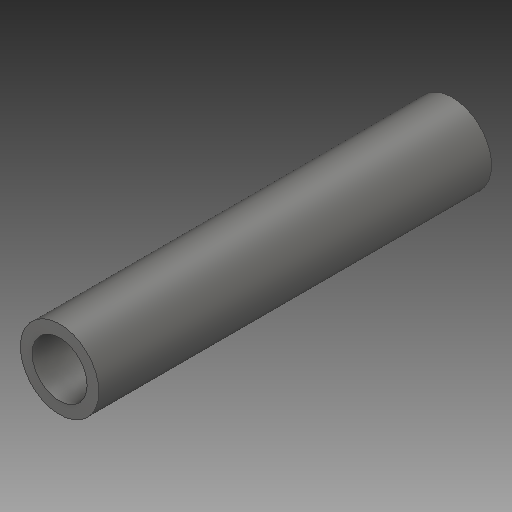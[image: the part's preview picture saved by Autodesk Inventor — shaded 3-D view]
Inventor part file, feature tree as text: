
AUTODESK INVENTOR PART (.ipt)
format: ipt  version: 2019 (Build 230136000, 136)  size: 100,864 bytes
history: native  units: in
note: dims shown in document units (in); Inventor stores cm internally (conversion verified against a paired STEP export)
features: other x3, sketch x3
ambient origin geometry x8: Origin, YZ Plane, XZ Plane, XY Plane, X Axis, Y Axis, Z Axis, Center Point
bodies: Solid1 (feature_tree)
feature tree (6):
  other  "project rolller 1 part.ipt"
  other  "Solid2::project rolller 1 part.ipt"
  other  "TaggingFeature1"
  sketch  "Sketch5"  dims[d0=0.3937in]
  sketch  "Sketch6"
  sketch  "Sketch7"
